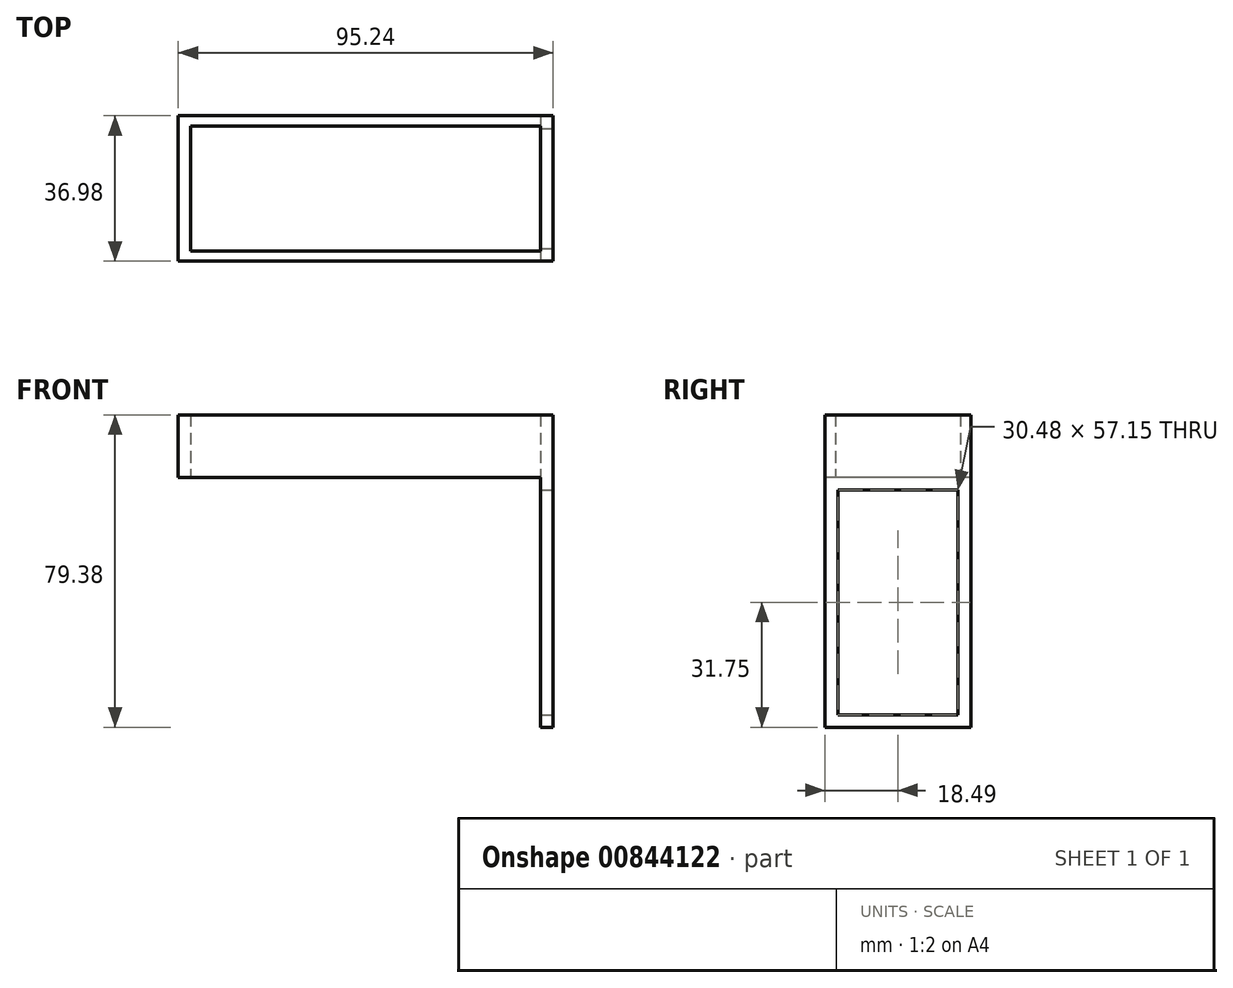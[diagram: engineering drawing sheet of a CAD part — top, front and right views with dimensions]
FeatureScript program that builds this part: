
annotation { "Feature Type Name" : "Feature", "Feature Type Description" : "" }
export const myFeature = defineFeature(function(context is Context, id is Id, definition is map)
    precondition{}
    {
        {
            var Q0;
            Q0=qCreatedBy(makeId("Top.planeOp"),FACE);
            var sketch = newSketch(context, id + "F0", { "sketchPlane" : qUnion([Q0])});
            skLineSegment(sketch, "E0.bottom", {"start": v(-44.45, 15.88) * mm, "end": v(44.45, 15.88) * mm});
            skLineSegment(sketch, "E0.top", {"start": v(-44.45, -15.88) * mm, "end": v(44.45, -15.88) * mm});
            skLineSegment(sketch, "E0.left", {"start": v(-44.45, 15.87) * mm, "end": v(-44.45, -15.88) * mm});
            skLineSegment(sketch, "E0.right", {"start": v(44.45, 15.88) * mm, "end": v(44.45, -15.87) * mm});
            skLineSegment(sketch, "E1", {"start": v(-44.45, 0) * mm, "end": v(0, 0) * mm});
            skLineSegment(sketch, "E2", {"start": v(44.45, 0) * mm, "end": v(0, 0) * mm});
            skLineSegment(sketch, "E3", {"start": v(0, 0) * mm, "end": v(0, 15.88) * mm});
            skLineSegment(sketch, "E4", {"start": v(0, 15.88) * mm, "end": v(0, 0) * mm});
            skLineSegment(sketch, "E5", {"start": v(0, 0) * mm, "end": v(0, -15.88) * mm});
            skLineSegment(sketch, "E6.bottom", {"start": v(-47.63, 18.5) * mm, "end": v(47.62, 18.5) * mm});
            skLineSegment(sketch, "E6.top", {"start": v(-47.62, -18.5) * mm, "end": v(47.62, -18.5) * mm});
            skLineSegment(sketch, "E6.left", {"start": v(-47.63, 18.5) * mm, "end": v(-47.63, -18.5) * mm});
            skLineSegment(sketch, "E6.right", {"start": v(47.63, 18.5) * mm, "end": v(47.63, -18.5) * mm});
            skLineSegment(sketch, "E7", {"start": v(-47.62, 18.5) * mm, "end": v(-44.45, 15.87) * mm});
            skLineSegment(sketch, "E8", {"start": v(-47.62, -18.5) * mm, "end": v(-44.45, -15.87) * mm});
            skLineSegment(sketch, "E9", {"start": v(47.62, -18.5) * mm, "end": v(44.45, -15.87) * mm});
            skLineSegment(sketch, "E10", {"start": v(47.62, 18.5) * mm, "end": v(44.45, 15.88) * mm});
            skSolve(sketch);
        }
        {
            var Q0;
            Q0=makeQuery(id+"F0.imprint","IMPRINT",FACE,{"disambiguationData":[TD([[makeQuery(id+"F0.imprint","IMPRINT",EDGE,{"derivedFrom":sQuery(id+"F0.wireOp",EDGE,"E6.bottom")}),-1.0]])]});
            var Q1;
            Q1=makeQuery(id+"F0.imprint","IMPRINT",FACE,{"disambiguationData":[TD([[makeQuery(id+"F0.imprint","IMPRINT",EDGE,{"derivedFrom":sQuery(id+"F0.wireOp",EDGE,"E6.left")}),1.0]])]});
            var Q2;
            Q2=makeQuery(id+"F0.imprint","IMPRINT",FACE,{"disambiguationData":[TD([[makeQuery(id+"F0.imprint","IMPRINT",EDGE,{"derivedFrom":sQuery(id+"F0.wireOp",EDGE,"E6.right")}),-1.0]])]});
            var Q3;
            Q3=makeQuery(id+"F0.imprint","IMPRINT",FACE,{"disambiguationData":[TD([[makeQuery(id+"F0.imprint","IMPRINT",EDGE,{"derivedFrom":sQuery(id+"F0.wireOp",EDGE,"E6.top")}),1.0]])]});
            extrude(context, id + "F1", {"entities" : qUnion([Q0, Q1, Q2, Q3]), "depth" : 15.88 * mm, "offsetDistance" : 25.4 * mm});
        }
        {
            var Q0;
            Q0=makeQuery(id+"F1.opExtrude","SWEPT_FACE",FACE,{"disambiguationData":[OSD([sQuery(id+"F0.wireOp",EDGE,"E6.right")])]});
            var sketch = newSketch(context, id + "F2", { "sketchPlane" : qUnion([Q0])});
            skLineSegment(sketch, "E11", {"start": v(-18.5, 0) * mm, "end": v(-18.5, -63.5) * mm});
            skLineSegment(sketch, "E12", {"start": v(-18.5, -63.5) * mm, "end": v(18.5, -63.5) * mm});
            skLineSegment(sketch, "E13", {"start": v(18.5, -63.5) * mm, "end": v(18.5, 0) * mm});
            skLineSegment(sketch, "E14", {"start": v(18.5, 0) * mm, "end": v(-18.5, 0) * mm});
            skLineSegment(sketch, "E15", {"start": v(18.5, 0) * mm, "end": v(18.5, -63.5) * mm});
            skLineSegment(sketch, "E16.bottom", {"start": v(15.24, -3.17) * mm, "end": v(-15.24, -3.17) * mm});
            skLineSegment(sketch, "E16.top", {"start": v(15.24, -60.33) * mm, "end": v(-15.24, -60.33) * mm});
            skLineSegment(sketch, "E16.left", {"start": v(15.24, -3.17) * mm, "end": v(15.24, -60.33) * mm});
            skLineSegment(sketch, "E16.right", {"start": v(-15.24, -3.17) * mm, "end": v(-15.24, -60.33) * mm});
            skLineSegment(sketch, "E17", {"start": v(-18.5, 0) * mm, "end": v(-15.24, -3.17) * mm});
            skLineSegment(sketch, "E18", {"start": v(-18.5, -63.5) * mm, "end": v(-15.24, -60.33) * mm});
            skLineSegment(sketch, "E19", {"start": v(18.5, -63.5) * mm, "end": v(15.24, -60.33) * mm});
            skSolve(sketch);
        }
        {
            var Q0;
            Q0=makeQuery(id+"F2.imprint","IMPRINT",FACE,{"disambiguationData":[TD([[makeQuery(id+"F2.imprint","IMPRINT",EDGE,{"derivedFrom":sQuery(id+"F2.wireOp",EDGE,"E14")}),1.0]])]});
            var Q1;
            Q1=makeQuery(id+"F2.imprint","IMPRINT",FACE,{"disambiguationData":[TD([[makeQuery(id+"F2.imprint","IMPRINT",EDGE,{"derivedFrom":sQuery(id+"F2.wireOp",EDGE,"E11")}),1.0]])]});
            var Q2;
            Q2=makeQuery(id+"F2.imprint","IMPRINT",FACE,{"disambiguationData":[TD([[makeQuery(id+"F2.imprint","IMPRINT",EDGE,{"derivedFrom":sQuery(id+"F2.wireOp",EDGE,"E12")}),1.0]])]});
            extrude(context, id + "F3", {"entities" : qUnion([Q0, Q1, Q2]), "operationType" : NewBodyOperationType.ADD, "oppositeDirection" : true, "depth" : 3.17 * mm, "offsetDistance" : 25.4 * mm});
        }
    });
